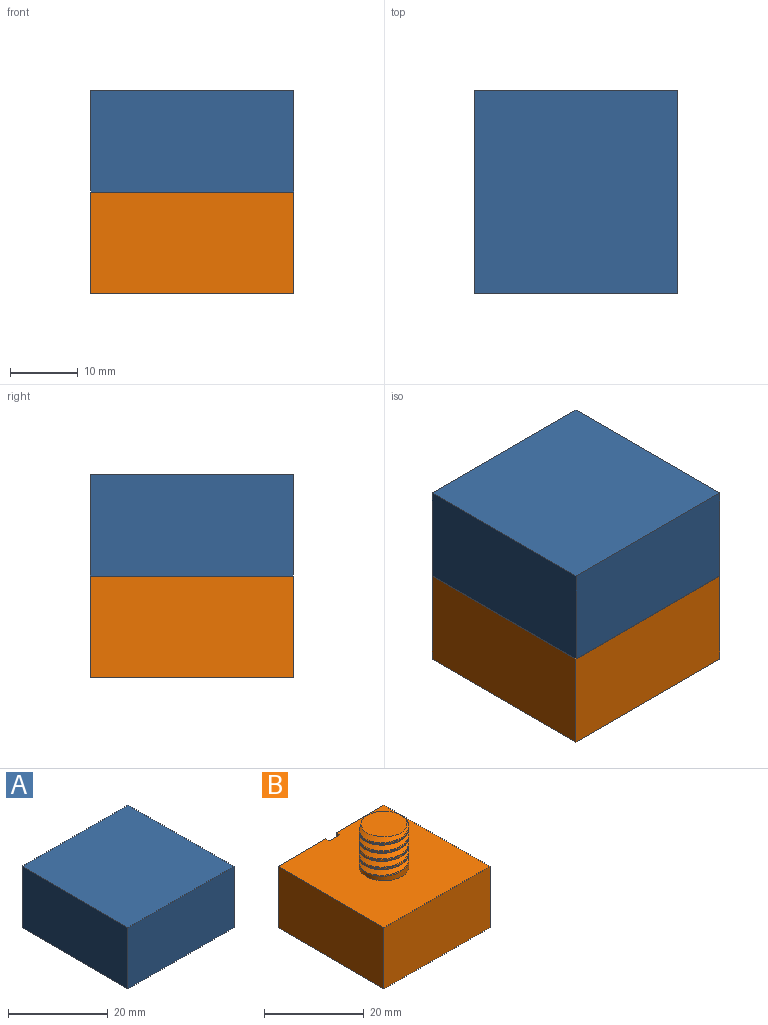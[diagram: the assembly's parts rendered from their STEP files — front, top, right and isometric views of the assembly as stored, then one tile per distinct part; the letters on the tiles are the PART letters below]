
ASSEMBLY  parts=2 mates=1
PART A: 22 faces, bbox 30x30x15.2 mm
  f0: plane 30.01x30.01mm, normal (0,0,-1), area 815.5mm2, adj f1,f2,f3,f4,f6,f10,f12,f14
  f1: plane 30x15mm, normal (1,0,0), area 450mm2, adj f0,f2,f4,f5
  f2: plane 30x15mm, normal (0,1,0), area 423.6mm2, adj f0,f1,f3,f5,f15,f16,f18,f19
  f3: plane 30x15mm, normal (-1,0,0), area 450mm2, adj f0,f2,f4,f5
  f4: plane 30x15mm, normal (0,-1,0), area 450mm2, adj f0,f1,f3,f5
  f5: plane 30x30mm, normal (0,0,1), area 900mm2, adj f1,f2,f3,f4
  f6: bspline ~10.24x10.22mm, area 15.8mm2, adj f0,f10,f11,f14
  f7: bspline ~10.03x9.93mm, area 15.4mm2, adj f11,f12,f14
  f8: bspline ~9.92x9.92mm, area 13.3mm2, adj f11,f12,f13
  f9: bspline ~10.23x10.23mm, area 13.3mm2, adj f10,f11,f12,f13
  f10: cylinder r=5.1mm len=10.2mm, axis (0,0,-1), area 62.2mm2, adj f0,f6,f9,f11,f12
  f11: plane 9.4x9.39mm, normal (0,0,-1), area 68.6mm2, adj f6,f7,f8,f9,f10,f13,f14
  f12: plane 1.62x1.2mm, normal (0,-1,0), area 0.9mm2, adj f0,f7,f8,f9,f10,f13,f14
  f13: bspline ~10.02x10.02mm, area 27.8mm2, adj f8,f9,f11,f12
  f14: bspline ~10.29x9.99mm, area 32.7mm2, adj f0,f6,f7,f11,f12
  f15: plane 2.74x1mm, normal (1,0,0), area 2.7mm2, adj f0,f2,f17,f18
  f16: plane 2.74x1mm, normal (-1,0,0), area 2.7mm2, adj f0,f2,f17,f21
  f17: plane 8.16x6.75mm, normal (0,1,0), area 26.4mm2, adj f0,f15,f16,f18,f19,f20,f21
  f18: plane 1.9x1mm, normal (0,0,1), area 1.9mm2, adj f2,f15,f17,f19
  f19: plane 5.42x3.37mm, normal (0.85,0,-0.53), area 6.4mm2, adj f2,f17,f18,f20
  f20: plane 5.42x3.37mm, normal (-0.85,0,-0.53), area 6.4mm2, adj f2,f17,f19,f21
  f21: plane 1.9x1mm, normal (0,0,1), area 1.9mm2, adj f2,f16,f17,f20
PART B: 17 faces, bbox 30.7x30.7x26.5 mm
  f0: plane 30.01x30.01mm, normal (0,0,1), area 818.5mm2, adj f1,f3,f4,f5,f6,f8,f12,f13
  f1: cylinder r=5mm len=10mm, axis (0,0,-1), area 60.5mm2, adj f0,f7,f8,f11,f12
  f2: plane 30x30mm, normal (0,0,-1), area 900mm2, adj f3,f4,f5,f6
  f3: plane 30x15mm, normal (0,-1,0), area 450mm2, adj f0,f2,f4,f6
  f4: plane 30x15mm, normal (-1,0,0), area 450mm2, adj f0,f2,f3,f5
  f5: plane 30x15mm, normal (0,1,0), area 427.5mm2, adj f0,f2,f4,f6,f13,f14,f15
  f6: plane 30x15mm, normal (1,0,0), area 450mm2, adj f0,f2,f3,f5
  f7: plane 9.81x9.8mm, normal (0,0,1), area 64.5mm2, adj f1,f9,f10,f11,f12
  f8: plane 1.62x1.3mm, normal (0,1,0), area 1mm2, adj f0,f1,f9,f10,f11,f12
  f9: bspline ~11.55x10.75mm, area 180.2mm2, adj f7,f8,f10,f12
  f10: bspline ~11.55x10.08mm, area 166.5mm2, adj f7,f8,f9,f11
  f11: bspline ~10.02x10.02mm, area 27.8mm2, adj f1,f7,f8,f10
  f12: bspline ~10.47x10.02mm, area 32.7mm2, adj f0,f1,f7,f8,f9
  f13: plane 7.61x1mm, normal (1,0,0), area 7.6mm2, adj f0,f5,f15,f16
  f14: plane 7.61x1mm, normal (-1,0,0), area 7.6mm2, adj f0,f5,f15,f16
  f15: plane 2.96x1mm, normal (0,0,1), area 3mm2, adj f5,f13,f14,f16
  f16: plane 7.61x2.96mm, normal (0,1,0), area 22.5mm2, adj f0,f13,f14,f15
PLACE A t=(0.67,-2.14,-1.7)mm
PLACE B t=(0.61,-2.19,-1.7)mm
MATE cylindrical A.f11 <-> B.f7  axis (0,0,-1) through (1.03,-1.78,8.3)mm
